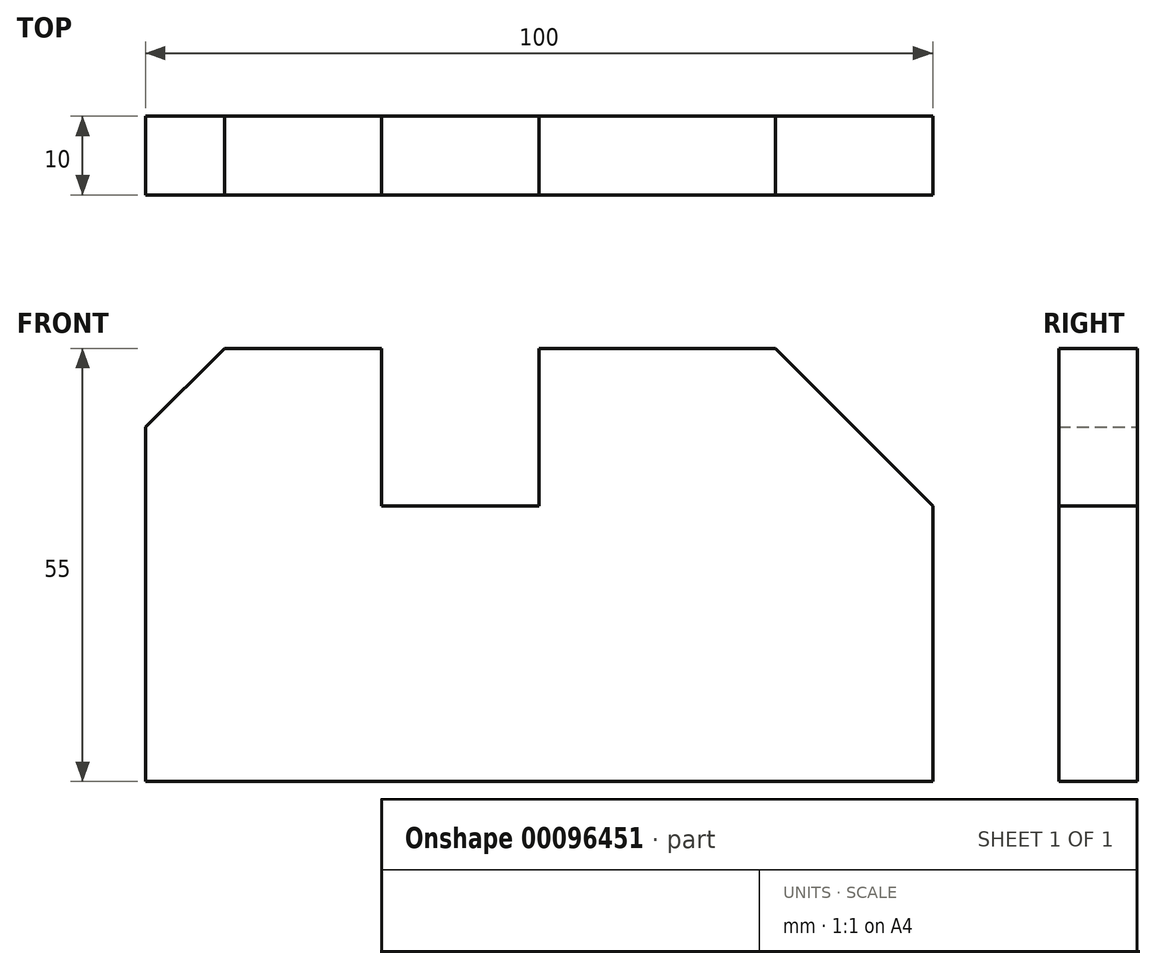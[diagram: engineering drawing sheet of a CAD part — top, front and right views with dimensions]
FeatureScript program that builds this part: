
annotation { "Feature Type Name" : "Feature", "Feature Type Description" : "" }
export const myFeature = defineFeature(function(context is Context, id is Id, definition is map)
    precondition{}
    {
        {
            var Q0;
            Q0=qCreatedBy(makeId("Front.planeOp"),FACE);
            var sketch = newSketch(context, id + "F0", { "sketchPlane" : qUnion([Q0])});
            skLineSegment(sketch, "E0", {"start": v(0, 0) * mm, "end": v(100, 0) * mm});
            skLineSegment(sketch, "E1", {"start": v(100, 0) * mm, "end": v(100, 35) * mm});
            skLineSegment(sketch, "E2", {"start": v(0, 0) * mm, "end": v(0, 45) * mm});
            skLineSegment(sketch, "E3", {"start": v(0, 45) * mm, "end": v(10, 55) * mm});
            skLineSegment(sketch, "E4", {"start": v(10, 55) * mm, "end": v(30, 55) * mm});
            skLineSegment(sketch, "E5", {"start": v(30, 55) * mm, "end": v(30, 35) * mm});
            skLineSegment(sketch, "E6", {"start": v(30, 35) * mm, "end": v(50, 35) * mm});
            skLineSegment(sketch, "E7", {"start": v(50, 35) * mm, "end": v(50, 55) * mm});
            skLineSegment(sketch, "E8", {"start": v(50, 55) * mm, "end": v(80, 55) * mm});
            skLineSegment(sketch, "E9", {"start": v(80, 55) * mm, "end": v(100, 35) * mm});
            skLineSegment(sketch, "E10", {"start": v(30, 55) * mm, "end": v(50, 55) * mm, "construction": true});
            skSolve(sketch);
        }
        {
            var Q0;
            Q0=makeQuery(id+"F0.imprint","IMPRINT",FACE,{"disambiguationData":[TD([[makeQuery(id+"F0.imprint","IMPRINT",EDGE,{"derivedFrom":sQuery(id+"F0.wireOp",EDGE,"E0")}),1.0]])]});
            extrude(context, id + "F1", {"entities" : qUnion([Q0]), "depth" : 10 * mm});
        }
    });
